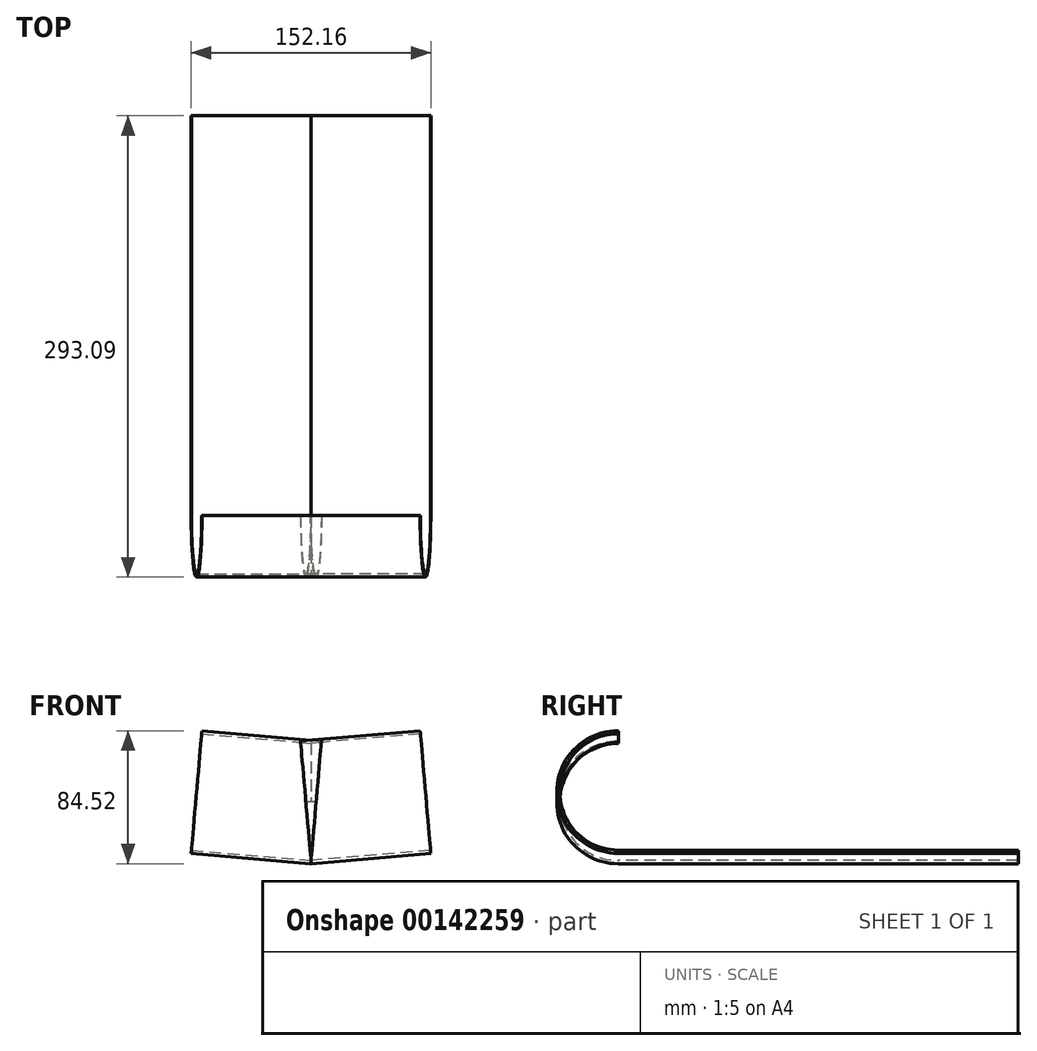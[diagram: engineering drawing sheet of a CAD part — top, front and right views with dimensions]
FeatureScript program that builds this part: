
annotation { "Feature Type Name" : "Feature", "Feature Type Description" : "" }
export const myFeature = defineFeature(function(context is Context, id is Id, definition is map)
    precondition{}
    {
        {
            var Q0;
            Q0=qCreatedBy(makeId("Right.planeOp"),FACE);
            var sketch = newSketch(context, id + "F0", { "sketchPlane" : qUnion([Q0])});
            skLineSegment(sketch, "E0", {"start": v(254, 0) * mm, "end": v(0, 0) * mm});
            skLineSegment(sketch, "E1", {"start": v(254, 0) * mm, "end": v(254, 2) * mm});
            skLineSegment(sketch, "E2", {"start": v(254, 2) * mm, "end": v(0, 2) * mm});
            skArc(sketch, "E3", {"start": v(0, 76.2) * mm, "mid": v(-37.1, 39.1) * mm, "end": v(0, 2) * mm});
            skArc(sketch, "E4", {"start": v(0, 78.18) * mm, "mid": v(-39.1, 39.1) * mm, "end": v(0, 0) * mm});
            skLineSegment(sketch, "E5", {"start": v(0, 78.18) * mm, "end": v(0, 76.2) * mm});
            skSolve(sketch);
        }
        {
            var Q0;
            Q0 = qSketchRegion(id + "F0", true);
            extrude(context, id + "F1", {"entities" : qUnion([Q0]), "depth" : 76.2 * mm});
        }
        {
            var Q0;
            Q0 = qSketchRegion(id + "F0", true);
            extrude(context, id + "F2", {"entities" : qUnion([Q0]), "oppositeDirection" : true, "depth" : 76.2 * mm});
        }
        {
            var Q0;
            Q0=makeQuery(id+"F1.opExtrude","SWEPT_BODY",BODY,{"disambiguationData":[OSD([sQuery(id+"F0.wireOp",EDGE,"E0"),sQuery(id+"F0.wireOp",EDGE,"E1"),sQuery(id+"F0.wireOp",EDGE,"E2"),sQuery(id+"F0.wireOp",EDGE,"E3"),sQuery(id+"F0.wireOp",EDGE,"E4"),sQuery(id+"F0.wireOp",EDGE,"E5")])]});
            var Q1;
            Q1=makeQuery(id+"F1.opExtrude","CAP_EDGE",EDGE,{"disambiguationData":[OSD([sQuery(id+"F0.wireOp",EDGE,"E2")])],"isStart":true});
            transform(context, id + "F3", {"entities" : qUnion([Q0]), "transformType" : TransformType.ROTATION, "transformAxis" : qUnion([Q1]), "angle" : 5 * degree, "makeCopy" : false});
        }
        {
            var Q0;
            Q0=makeQuery(id+"F2.opExtrude","SWEPT_BODY",BODY,{"disambiguationData":[OSD([sQuery(id+"F0.wireOp",EDGE,"E0"),sQuery(id+"F0.wireOp",EDGE,"E1"),sQuery(id+"F0.wireOp",EDGE,"E2"),sQuery(id+"F0.wireOp",EDGE,"E3"),sQuery(id+"F0.wireOp",EDGE,"E4"),sQuery(id+"F0.wireOp",EDGE,"E5")])]});
            var Q1;
            Q1=makeQuery(id+"F1.opExtrude","CAP_EDGE",EDGE,{"disambiguationData":[OSD([sQuery(id+"F0.wireOp",EDGE,"E2")])],"isStart":true});
            transform(context, id + "F4", {"entities" : qUnion([Q0]), "transformType" : TransformType.ROTATION, "transformAxis" : qUnion([Q1]), "angle" : 5 * degree, "oppositeDirection" : true, "makeCopy" : false});
        }
        {
            var Q0;
            Q0=makeQuery(id+"F1.opExtrude","CAP_FACE",FACE,{"disambiguationData":[OSD([sQuery(id+"F0.wireOp",EDGE,"E0"),sQuery(id+"F0.wireOp",EDGE,"E1"),sQuery(id+"F0.wireOp",EDGE,"E2"),sQuery(id+"F0.wireOp",EDGE,"E3"),sQuery(id+"F0.wireOp",EDGE,"E4"),sQuery(id+"F0.wireOp",EDGE,"E5")])],"isStart":true});
            var Q1;
            Q1=makeQuery(id+"F2.opExtrude","SWEPT_FACE",FACE,{"disambiguationData":[OSD([sQuery(id+"F0.wireOp",EDGE,"E3")])]});
            extrude(context, id + "F5", {"entities" : qUnion([Q0]), "operationType" : NewBodyOperationType.REMOVE, "endBound" : BoundingType.UP_TO_SURFACE, "oppositeDirection" : true, "endBoundEntityFace" : qUnion([Q1]), "depth" : 25.4 * mm});
        }
        {
            var Q0;
            Q0=makeQuery(id+"F2.opExtrude","CAP_FACE",FACE,{"disambiguationData":[OSD([sQuery(id+"F0.wireOp",EDGE,"E0"),sQuery(id+"F0.wireOp",EDGE,"E1"),sQuery(id+"F0.wireOp",EDGE,"E2"),sQuery(id+"F0.wireOp",EDGE,"E3"),sQuery(id+"F0.wireOp",EDGE,"E4"),sQuery(id+"F0.wireOp",EDGE,"E5")])],"isStart":true});
            var Q1;
            Q1=makeQuery(id+"F1.opExtrude","SWEPT_FACE",FACE,{"disambiguationData":[OSD([sQuery(id+"F0.wireOp",EDGE,"E3")])]});
            extrude(context, id + "F6", {"entities" : qUnion([Q0]), "operationType" : NewBodyOperationType.REMOVE, "endBound" : BoundingType.UP_TO_SURFACE, "oppositeDirection" : true, "endBoundEntityFace" : qUnion([Q1]), "depth" : 25.4 * mm});
        }
    });
